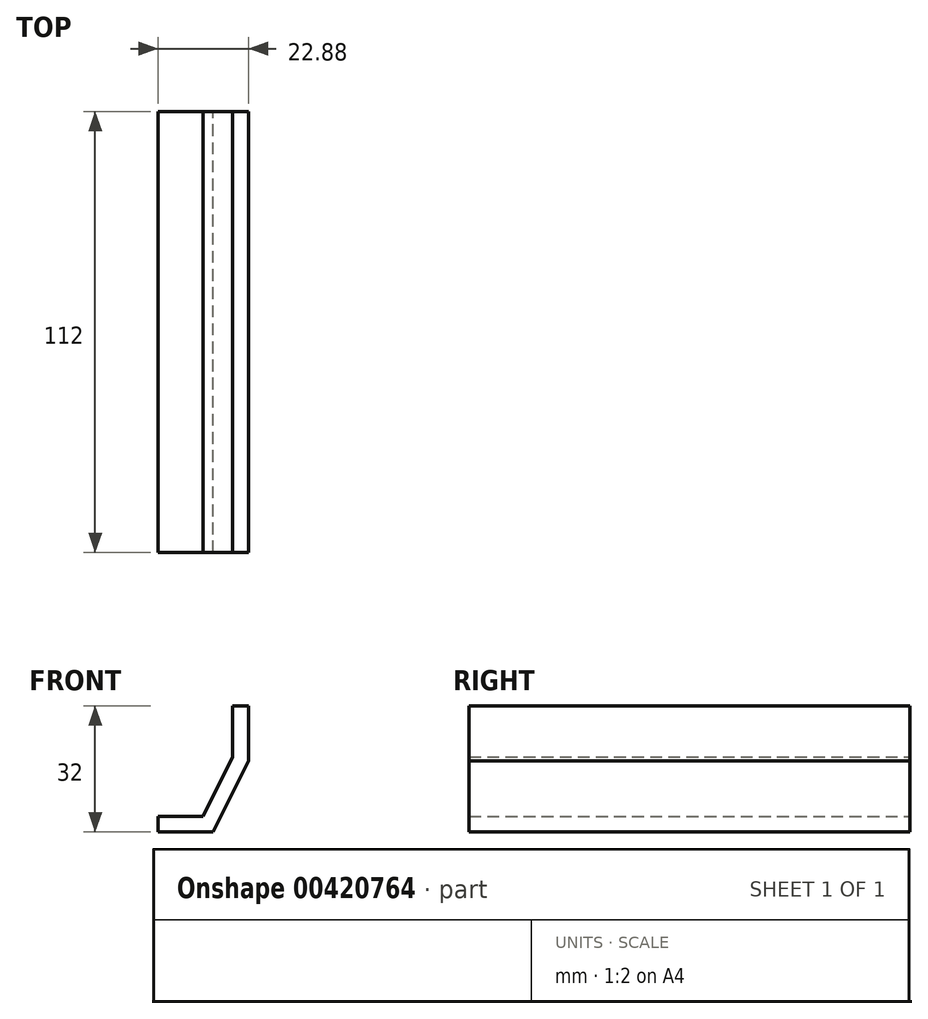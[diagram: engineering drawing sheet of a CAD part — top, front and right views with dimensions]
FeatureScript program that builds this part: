
annotation { "Feature Type Name" : "Feature", "Feature Type Description" : "" }
export const myFeature = defineFeature(function(context is Context, id is Id, definition is map)
    precondition{}
    {
        {
            var Q0;
            Q0=qCreatedBy(makeId("Front.planeOp"),FACE);
            var sketch = newSketch(context, id + "F0", { "sketchPlane" : qUnion([Q0])});
            skLineSegment(sketch, "E0", {"start": v(-30.18, 9.7) * mm, "end": v(-30.18, 13.7) * mm});
            skLineSegment(sketch, "E1", {"start": v(-30.18, 13.7) * mm, "end": v(-18.76, 13.7) * mm});
            skLineSegment(sketch, "E2", {"start": v(-18.76, 13.7) * mm, "end": v(-11.3, 28.75) * mm});
            skLineSegment(sketch, "E3", {"start": v(-7.3, 27.8) * mm, "end": v(-16.28, 9.7) * mm});
            skLineSegment(sketch, "E4", {"start": v(-11.3, 28.75) * mm, "end": v(-11.3, 41.7) * mm});
            skLineSegment(sketch, "E5", {"start": v(-11.3, 41.7) * mm, "end": v(-7.3, 41.7) * mm});
            skLineSegment(sketch, "E6", {"start": v(-7.3, 41.7) * mm, "end": v(-7.3, 27.8) * mm});
            skLineSegment(sketch, "E7", {"start": v(-16.28, 9.7) * mm, "end": v(-30.18, 9.7) * mm});
            skSolve(sketch);
        }
        {
            var Q0;
            {var subQ0=sQuery(id+"F0.wireOp",EDGE,"E0");Q0=makeQuery(id+"F0.imprint","IMPRINT",FACE,{"disambiguationData":[TD([[makeQuery(id+"F0.imprint","IMPRINT",EDGE,{"derivedFrom":subQ0}),-1.0]])]});}
            extrude(context, id + "F1", {"entities" : qUnion([Q0]), "depth" : 112 * mm});
        }
    });
